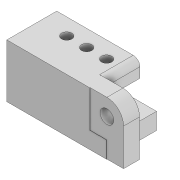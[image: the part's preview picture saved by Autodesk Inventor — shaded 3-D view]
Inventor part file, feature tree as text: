
AUTODESK INVENTOR PART (.ipt)
format: ipt  version: 2022 (Build 260153000, 153)  size: 188,928 bytes
history: native  units: mm
features: extrude x8, sketch x5, projected_geometry x3, pattern_linear x2, fillet x2
ambient origin geometry x8: Origin, YZ Plane, XZ Plane, XY Plane, X Axis, Y Axis, Z Axis, Center Point
bodies: Solid1 (feature_tree)
feature tree (20):
  sketch  "Sketch2"  dims[d0=3.1mm d1=10.0mm]
  extrude  "Extrusion1"  Depth=10.0mm
  extrude  "Extrusion2"  Depth=30.0mm
  pattern_linear  "Rectangular Pattern1"  Count1=3 Spacing1=6.0mm
  pattern_linear  "Rectangular Pattern2"  Count1=2 Spacing1=11.1mm
  sketch  "Sketch3"  dims[d2=5.0mm d3=30.0mm]
  extrude  "Extrusion3"  Depth=5.0mm TaperAngle=0.0deg
  extrude  "Extrusion4"  Depth=5.0mm TaperAngle=0.0deg
  extrude  "Extrusion5"  Depth=2.0mm TaperAngle=0.0deg
  extrude  "Extrusion6"  Depth=2.0mm
  fillet  "Fillet1"  Radius=10.0mm
  extrude  "Extrusion7"  Depth=5.0mm
  extrude  "Extrusion8"  Depth=5.0mm
  fillet  "Fillet2"  Radius=10.0mm
  sketch  "Sketch4"  dims[d4=10.0mm]
  sketch  "Sketch5"  dims[d5=5.0mm d6=0.0mm]
  projected_geometry  "Projected Loop1"
  sketch  "Sketch6"  dims[d7=10.0mm d8=0.0mm d9=30.0mm d11=6.0mm d12=20.0mm d14=11.1mm d18=5.0mm d19=0.0mm d20=5.0mm d21=0.0mm d22=100.0mm d23=0.0mm d28=4.1mm d29=10.0mm d31=5.0mm d32=5.0mm d33=10.0mm d34=0.0mm d35=5.0mm d36=0.1mm d37=0.0mm d38=0.1mm d39=0.0mm d40=2.0mm]
  projected_geometry  "Projected Loop2"
  projected_geometry  "Project Cut Edges1"
